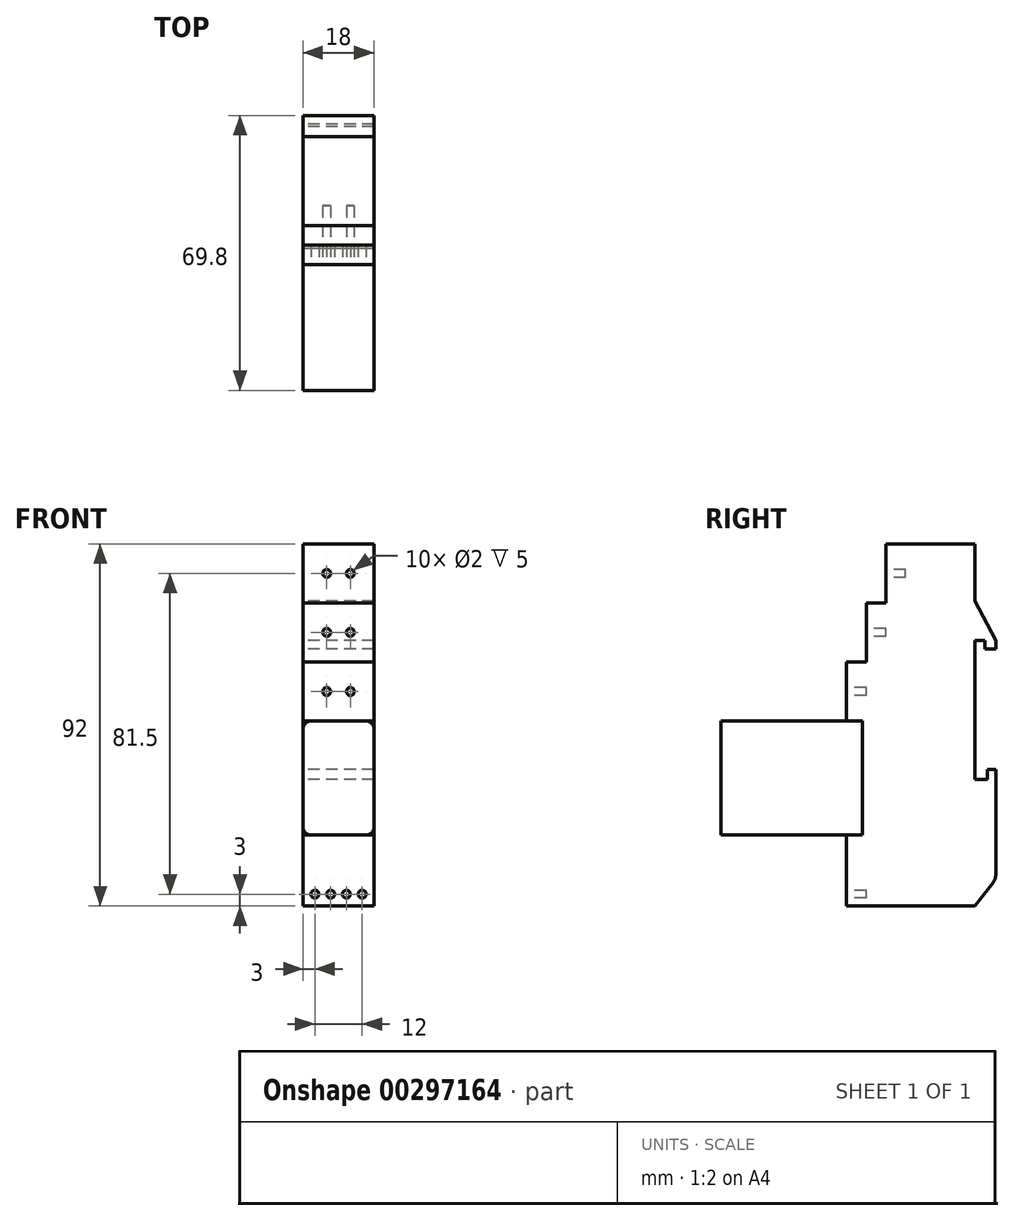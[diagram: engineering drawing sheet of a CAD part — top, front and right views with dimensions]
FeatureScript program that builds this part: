
annotation { "Feature Type Name" : "Feature", "Feature Type Description" : "" }
export const myFeature = defineFeature(function(context is Context, id is Id, definition is map)
    precondition{}
    {
        {
            var Q0;
            Q0=qCreatedBy(makeId("Right.planeOp"),FACE);
            var sketch = newSketch(context, id + "F0", { "sketchPlane" : qUnion([Q0])});
            skLineSegment(sketch, "E0", {"start": v(0, 35.4) * mm, "end": v(2.53, 35.4) * mm});
            skLineSegment(sketch, "E1", {"start": v(2.53, 35.4) * mm, "end": v(2.53, 33.23) * mm});
            skLineSegment(sketch, "E2", {"start": v(2.53, 33.23) * mm, "end": v(5.3, 33.23) * mm});
            skLineSegment(sketch, "E3", {"start": v(5.3, 33.23) * mm, "end": v(5.3, 35.4) * mm});
            skLineSegment(sketch, "E4", {"start": v(5.3, 35.4) * mm, "end": v(0, 45.4) * mm});
            skLineSegment(sketch, "E5", {"start": v(0, 45.4) * mm, "end": v(0, 59.9) * mm});
            skLineSegment(sketch, "E6", {"start": v(0, 59.9) * mm, "end": v(-22.6, 59.9) * mm});
            skLineSegment(sketch, "E7", {"start": v(-22.6, 59.9) * mm, "end": v(-22.6, 44.9) * mm});
            skLineSegment(sketch, "E8", {"start": v(-32.6, -32.1) * mm, "end": v(0, -32.1) * mm});
            skLineSegment(sketch, "E9", {"start": v(0, -32.1) * mm, "end": v(4.67, -26.07) * mm});
            skLineSegment(sketch, "E10", {"start": v(5.3, -24.23) * mm, "end": v(5.3, 0) * mm});
            skLineSegment(sketch, "E11", {"start": v(3.13, 0) * mm, "end": v(0, 0) * mm});
            skPoint(sketch, "E12.visualSharp", {"position": v(5.3, -25.26) * mm});
            skArc(sketch, "E12.filletArc", {"start": v(4.67, -26.07) * mm, "mid": v(5.14, -25.2) * mm, "end": v(5.3, -24.23) * mm});
            skLineSegment(sketch, "E13", {"start": v(5.3, 0) * mm, "end": v(5.3, 2.54) * mm});
            skLineSegment(sketch, "E14", {"start": v(5.3, 2.54) * mm, "end": v(3.13, 2.54) * mm});
            skLineSegment(sketch, "E15", {"start": v(3.13, 2.54) * mm, "end": v(3.13, 0) * mm});
            skLineSegment(sketch, "E16", {"start": v(0, 0) * mm, "end": v(0, 35.4) * mm});
            skPoint(sketch, "E17.orphan", {"position": v(0, 35.4) * mm});
            skPoint(sketch, "E18.end.orphan", {"position": v(-16.09, 66) * mm});
            skLineSegment(sketch, "E19", {"start": v(-22.6, 44.9) * mm, "end": v(-27.6, 44.9) * mm});
            skLineSegment(sketch, "E20", {"start": v(-27.6, 44.9) * mm, "end": v(-27.6, 29.9) * mm});
            skLineSegment(sketch, "E21", {"start": v(-27.6, 29.9) * mm, "end": v(-32.6, 29.9) * mm});
            skLineSegment(sketch, "E22", {"start": v(-32.6, 29.9) * mm, "end": v(-32.6, 14.9) * mm});
            skPoint(sketch, "E23.start.orphan", {"position": v(-16.09, 43.2) * mm});
            skLineSegment(sketch, "E24", {"start": v(-32.6, 14.9) * mm, "end": v(-28.5, 14.9) * mm});
            skLineSegment(sketch, "E25", {"start": v(-28.5, 14.9) * mm, "end": v(-28.5, -14.1) * mm});
            skLineSegment(sketch, "E26", {"start": v(-28.5, -14.1) * mm, "end": v(-32.6, -14.1) * mm});
            skLineSegment(sketch, "E27", {"start": v(-32.6, -14.1) * mm, "end": v(-32.6, -32.1) * mm});
            skSolve(sketch);
        }
        {
            var Q0;
            Q0=makeQuery(id+"F0.imprint","IMPRINT",FACE,{"disambiguationData":[TD([[makeQuery(id+"F0.imprint","IMPRINT",EDGE,{"derivedFrom":sQuery(id+"F0.wireOp",EDGE,"E0")}),1.0]])]});
            extrude(context, id + "F1", {"entities" : qUnion([Q0]), "depth" : 18 * mm, "symmetric" : true});
        }
        {
            var Q0;
            Q0=makeQuery(id+"F1.opExtrude","SWEPT_FACE",FACE,{"disambiguationData":[OSD([sQuery(id+"F0.wireOp",EDGE,"E7")])]});
            var sketch = newSketch(context, id + "F2", { "sketchPlane" : qUnion([Q0])});
            skLineSegment(sketch, "E28", {"start": v(0, 59.9) * mm, "end": v(0, 44.9) * mm});
            skCircle(sketch, "E29", {"center": v(-3, 52.4) * mm, "radius": 1 * mm});
            skCircle(sketch, "E30", {"center": v(3, 52.4) * mm, "radius": 1 * mm});
            skSolve(sketch);
        }
        {
            var Q0;
            Q0=makeQuery(id+"F2.imprint","IMPRINT",FACE,{"disambiguationData":[TD([[makeQuery(id+"F2.imprint","IMPRINT",EDGE,{"derivedFrom":sQuery(id+"F2.wireOp",EDGE,"E29")}),1.0]])]});
            var Q1;
            Q1=makeQuery(id+"F2.imprint","IMPRINT",FACE,{"disambiguationData":[TD([[makeQuery(id+"F2.imprint","IMPRINT",EDGE,{"derivedFrom":sQuery(id+"F2.wireOp",EDGE,"E30")}),1.0]])]});
            extrude(context, id + "F3", {"entities" : qUnion([Q0, Q1]), "operationType" : NewBodyOperationType.REMOVE, "oppositeDirection" : true, "depth" : 5 * mm});
        }
        {
            var Q0;
            Q0=makeQuery(id+"F1.opExtrude","SWEPT_FACE",FACE,{"disambiguationData":[OSD([sQuery(id+"F0.wireOp",EDGE,"E20")])]});
            var sketch = newSketch(context, id + "F4", { "sketchPlane" : qUnion([Q0])});
            skCircle(sketch, "E31", {"center": v(-3, 37.4) * mm, "radius": 1 * mm});
            skCircle(sketch, "E32", {"center": v(3, 37.4) * mm, "radius": 1 * mm});
            skSolve(sketch);
        }
        {
            var Q0;
            Q0=makeQuery(id+"F4.imprint","IMPRINT",FACE,{"disambiguationData":[TD([[makeQuery(id+"F4.imprint","IMPRINT",EDGE,{"derivedFrom":sQuery(id+"F4.wireOp",EDGE,"E31")}),1.0]])]});
            var Q1;
            Q1=makeQuery(id+"F4.imprint","IMPRINT",FACE,{"disambiguationData":[TD([[makeQuery(id+"F4.imprint","IMPRINT",EDGE,{"derivedFrom":sQuery(id+"F4.wireOp",EDGE,"E32")}),1.0]])]});
            extrude(context, id + "F5", {"entities" : qUnion([Q0, Q1]), "operationType" : NewBodyOperationType.REMOVE, "oppositeDirection" : true, "depth" : 5 * mm});
        }
        {
            var Q0;
            Q0=makeQuery(id+"F1.opExtrude","SWEPT_FACE",FACE,{"disambiguationData":[OSD([sQuery(id+"F0.wireOp",EDGE,"E22")])]});
            var sketch = newSketch(context, id + "F6", { "sketchPlane" : qUnion([Q0])});
            skCircle(sketch, "E33", {"center": v(3, 22.4) * mm, "radius": 1 * mm});
            skCircle(sketch, "E34", {"center": v(-3, 22.4) * mm, "radius": 1 * mm});
            skSolve(sketch);
        }
        {
            var Q0;
            Q0=makeQuery(id+"F6.imprint","IMPRINT",FACE,{"disambiguationData":[TD([[makeQuery(id+"F6.imprint","IMPRINT",EDGE,{"derivedFrom":sQuery(id+"F6.wireOp",EDGE,"E34")}),1.0]])]});
            var Q1;
            Q1=makeQuery(id+"F6.imprint","IMPRINT",FACE,{"disambiguationData":[TD([[makeQuery(id+"F6.imprint","IMPRINT",EDGE,{"derivedFrom":sQuery(id+"F6.wireOp",EDGE,"E33")}),1.0]])]});
            extrude(context, id + "F7", {"entities" : qUnion([Q0, Q1]), "operationType" : NewBodyOperationType.REMOVE, "oppositeDirection" : true, "depth" : 5 * mm});
        }
        {
            var Q0;
            Q0=makeQuery(id+"F1.opExtrude","SWEPT_FACE",FACE,{"disambiguationData":[OSD([sQuery(id+"F0.wireOp",EDGE,"E27")])]});
            var sketch = newSketch(context, id + "F8", { "sketchPlane" : qUnion([Q0])});
            skCircle(sketch, "E35", {"center": v(-6, -29.1) * mm, "radius": 1 * mm});
            skCircle(sketch, "E36", {"center": v(-2, -29.1) * mm, "radius": 1 * mm});
            skCircle(sketch, "E37", {"center": v(2, -29.1) * mm, "radius": 1 * mm});
            skCircle(sketch, "E38", {"center": v(6, -29.1) * mm, "radius": 1 * mm});
            skLineSegment(sketch, "E39", {"start": v(0, -32.1) * mm, "end": v(0, -14.1) * mm});
            skSolve(sketch);
        }
        {
            var Q0;
            Q0=makeQuery(id+"F8.imprint","IMPRINT",FACE,{"disambiguationData":[TD([[makeQuery(id+"F8.imprint","IMPRINT",EDGE,{"derivedFrom":sQuery(id+"F8.wireOp",EDGE,"E35")}),1.0]])]});
            var Q1;
            Q1=makeQuery(id+"F8.imprint","IMPRINT",FACE,{"disambiguationData":[TD([[makeQuery(id+"F8.imprint","IMPRINT",EDGE,{"derivedFrom":sQuery(id+"F8.wireOp",EDGE,"E36")}),1.0]])]});
            var Q2;
            Q2=makeQuery(id+"F8.imprint","IMPRINT",FACE,{"disambiguationData":[TD([[makeQuery(id+"F8.imprint","IMPRINT",EDGE,{"derivedFrom":sQuery(id+"F8.wireOp",EDGE,"E37")}),1.0]])]});
            var Q3;
            Q3=makeQuery(id+"F8.imprint","IMPRINT",FACE,{"disambiguationData":[TD([[makeQuery(id+"F8.imprint","IMPRINT",EDGE,{"derivedFrom":sQuery(id+"F8.wireOp",EDGE,"E38")}),1.0]])]});
            extrude(context, id + "F9", {"entities" : qUnion([Q0, Q1, Q2, Q3]), "operationType" : NewBodyOperationType.REMOVE, "oppositeDirection" : true, "depth" : 5 * mm});
        }
        {
            var Q0;
            Q0=makeQuery(id+"F1.opExtrude","SWEPT_FACE",FACE,{"disambiguationData":[OSD([sQuery(id+"F0.wireOp",EDGE,"E25")])]});
            var sketch = newSketch(context, id + "F10", { "sketchPlane" : qUnion([Q0])});
            skLineSegment(sketch, "E40", {"start": v(-9, 14.9) * mm, "end": v(9, 14.9) * mm});
            skLineSegment(sketch, "E41", {"start": v(9, 14.9) * mm, "end": v(9, -14.1) * mm});
            skLineSegment(sketch, "E42", {"start": v(9, -14.1) * mm, "end": v(-9, -14.1) * mm});
            skLineSegment(sketch, "E43", {"start": v(-9, -14.1) * mm, "end": v(-9, 14.9) * mm});
            skSolve(sketch);
        }
        {
            var Q0;
            Q0=makeQuery(id+"F10.imprint","IMPRINT",FACE,{"disambiguationData":[TD([[makeQuery(id+"F10.imprint","IMPRINT",EDGE,{"derivedFrom":sQuery(id+"F10.wireOp",EDGE,"E40")}),1.0]])]});
            extrude(context, id + "F11", {"entities" : qUnion([Q0]), "depth" : 36 * mm});
        }
        {
            var Q0;
            Q0=makeQuery(id+"F11.opExtrude","SWEPT_EDGE",EDGE,{"disambiguationData":[OSD([sQuery(id+"F10.wireOp",EDGE,"E40"),sQuery(id+"F10.wireOp",EDGE,"E41")])]});
            var Q1;
            Q1=makeQuery(id+"F11.opExtrude","SWEPT_EDGE",EDGE,{"disambiguationData":[OSD([sQuery(id+"F10.wireOp",EDGE,"E41"),sQuery(id+"F10.wireOp",EDGE,"E42")])]});
            var Q2;
            Q2=makeQuery(id+"F11.opExtrude","SWEPT_EDGE",EDGE,{"disambiguationData":[OSD([sQuery(id+"F10.wireOp",EDGE,"E42"),sQuery(id+"F10.wireOp",EDGE,"E43")])]});
            var Q3;
            Q3=makeQuery(id+"F11.opExtrude","SWEPT_EDGE",EDGE,{"disambiguationData":[OSD([sQuery(id+"F10.wireOp",EDGE,"E40"),sQuery(id+"F10.wireOp",EDGE,"E43")])]});
            fillet(context, id + "F12", {"entities" : qUnion([Q0, Q1, Q2, Q3]), "radius" : 2 * mm, "tangentPropagation" : true, "allowEdgeOverflow" : false});
        }
    });
